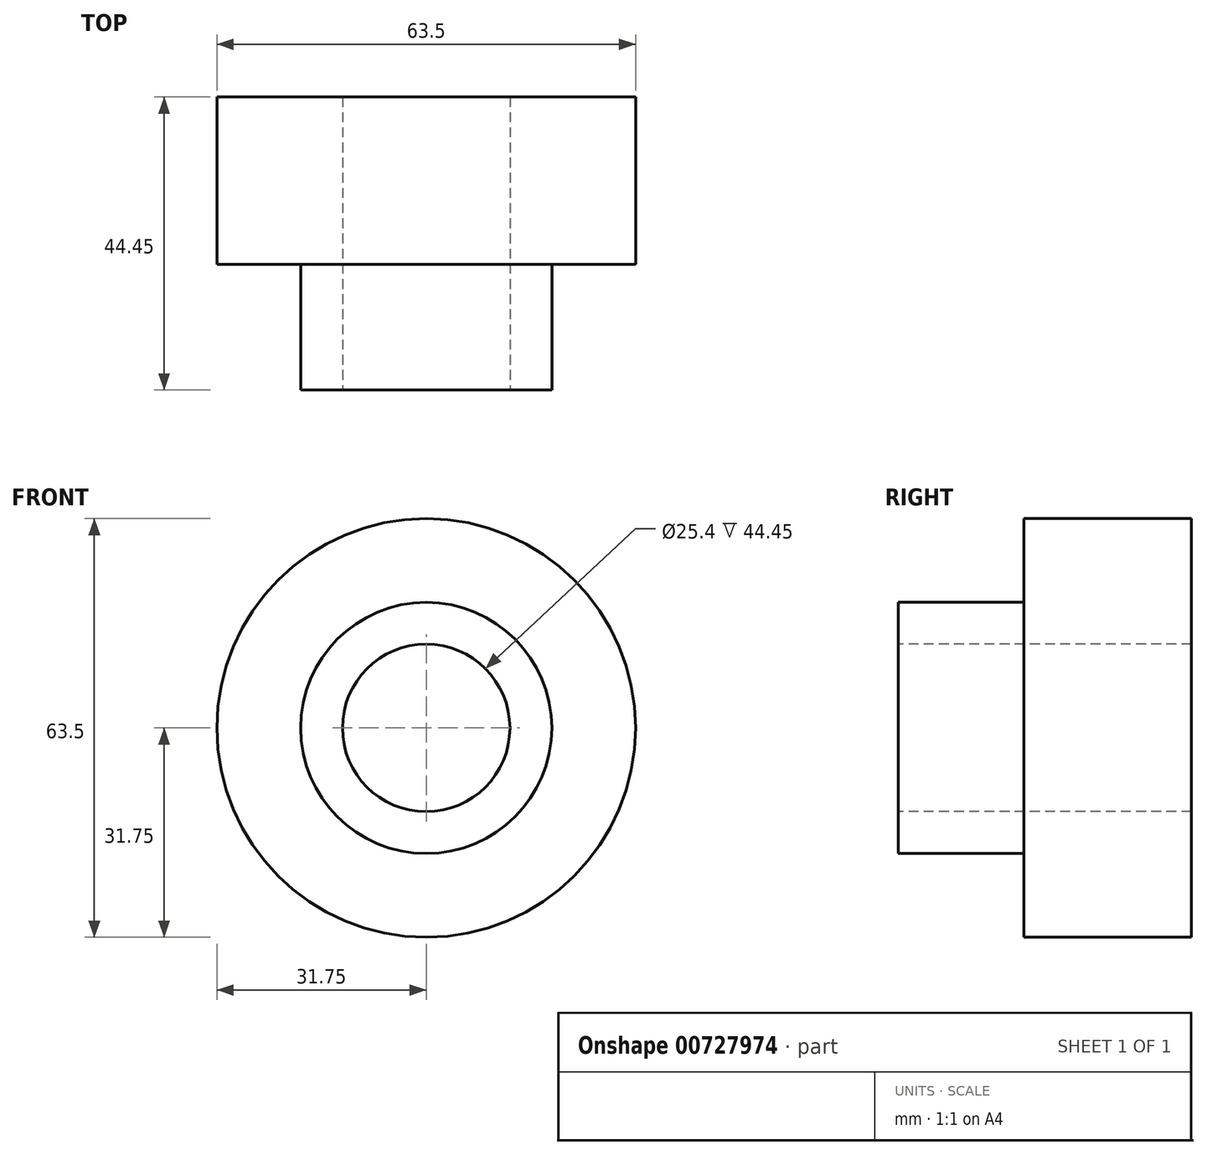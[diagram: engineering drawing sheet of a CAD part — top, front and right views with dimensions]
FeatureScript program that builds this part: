
annotation { "Feature Type Name" : "Feature", "Feature Type Description" : "" }
export const myFeature = defineFeature(function(context is Context, id is Id, definition is map)
    precondition{}
    {
        {
            var Q0;
            Q0=qCreatedBy(makeId("Front.planeOp"),FACE);
            var sketch = newSketch(context, id + "F0", { "sketchPlane" : qUnion([Q0])});
            skCircle(sketch, "E0", {"center": v(0, 0) * mm, "radius": 31.75 * mm});
            skSolve(sketch);
        }
        {
            var Q0;
            Q0=makeQuery(id+"F0.imprint","IMPRINT",FACE,{"disambiguationData":[TD([[makeQuery(id+"F0.imprint","IMPRINT",EDGE,{"derivedFrom":sQuery(id+"F0.wireOp",EDGE,"E0")}),1.0]])]});
            extrude(context, id + "F1", {"entities" : qUnion([Q0]), "depth" : 25.4 * mm, "offsetDistance" : 25.4 * mm});
        }
        {
            var Q0;
            Q0=makeQuery(id+"F1.opExtrude","CAP_FACE",FACE,{"disambiguationData":[OSD([sQuery(id+"F0.wireOp",EDGE,"E0")])],"isStart":false});
            var sketch = newSketch(context, id + "F2", { "sketchPlane" : qUnion([Q0])});
            skCircle(sketch, "E1", {"center": v(0, 0) * mm, "radius": 19.05 * mm});
            skSolve(sketch);
        }
        {
            var Q0;
            Q0=makeQuery(id+"F2.imprint","IMPRINT",FACE,{"disambiguationData":[TD([[makeQuery(id+"F2.imprint","IMPRINT",EDGE,{"derivedFrom":sQuery(id+"F2.wireOp",EDGE,"E1")}),1.0]])]});
            extrude(context, id + "F3", {"entities" : qUnion([Q0]), "operationType" : NewBodyOperationType.ADD, "depth" : 19.05 * mm, "offsetDistance" : 25.4 * mm});
        }
        {
            var Q0;
            Q0=makeQuery(id+"F3.opExtrude","CAP_FACE",FACE,{"disambiguationData":[OSD([sQuery(id+"F2.wireOp",EDGE,"E1")])],"isStart":false});
            var sketch = newSketch(context, id + "F4", { "sketchPlane" : qUnion([Q0])});
            skCircle(sketch, "E2", {"center": v(0, 0) * mm, "radius": 12.7 * mm});
            skSolve(sketch);
        }
        {
            var Q0;
            Q0=makeQuery(id+"F4.imprint","IMPRINT",FACE,{"disambiguationData":[TD([[makeQuery(id+"F4.imprint","IMPRINT",EDGE,{"derivedFrom":sQuery(id+"F4.wireOp",EDGE,"E2")}),1.0]])]});
            extrude(context, id + "F5", {"entities" : qUnion([Q0]), "operationType" : NewBodyOperationType.REMOVE, "oppositeDirection" : true, "depth" : 111 * mm, "offsetDistance" : 25.4 * mm});
        }
    });
